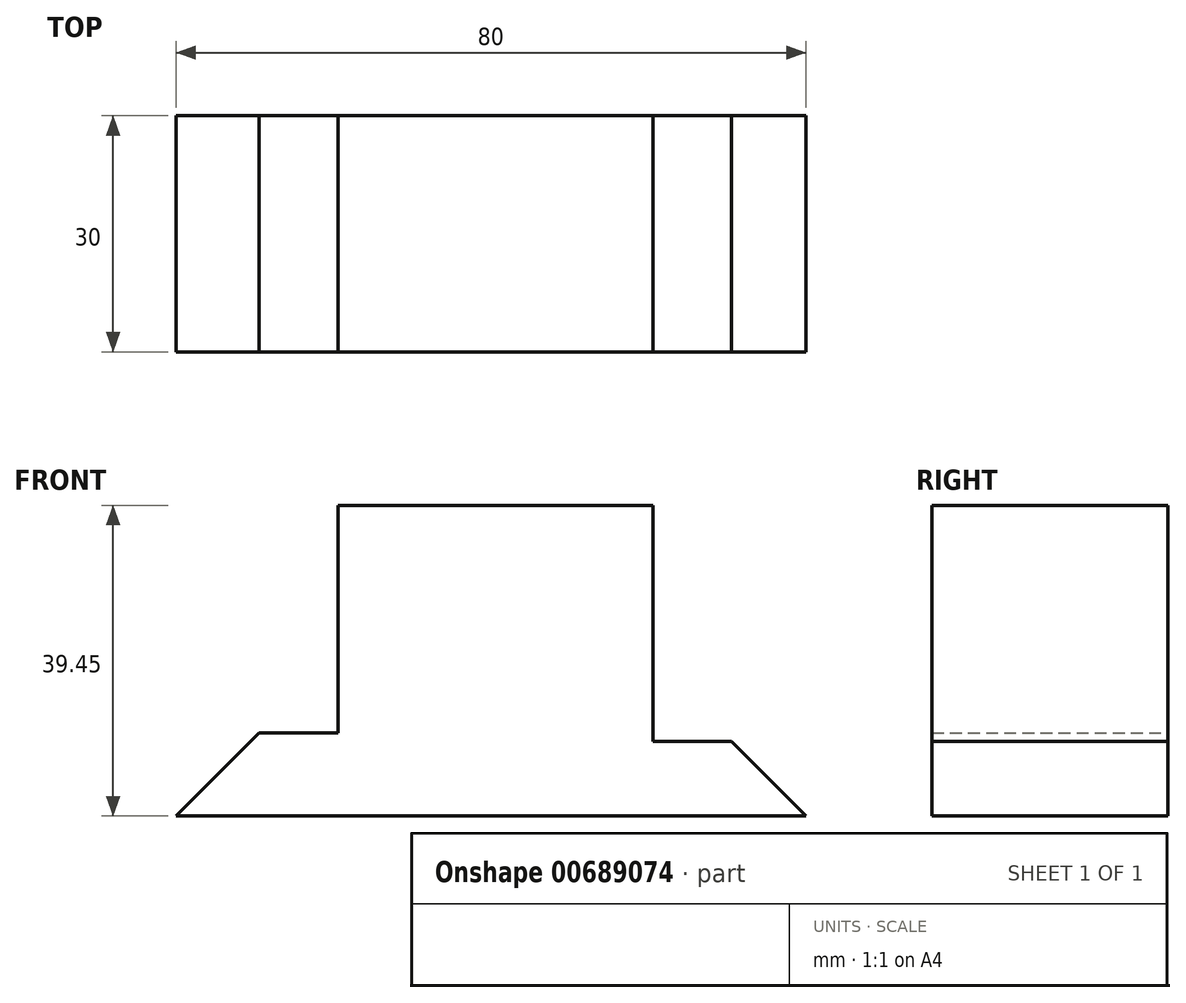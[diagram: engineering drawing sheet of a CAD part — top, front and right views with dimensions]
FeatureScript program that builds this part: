
annotation { "Feature Type Name" : "Feature", "Feature Type Description" : "" }
export const myFeature = defineFeature(function(context is Context, id is Id, definition is map)
    precondition{}
    {
        {
            var Q0;
            Q0=qCreatedBy(makeId("Front.planeOp"),FACE);
            var sketch = newSketch(context, id + "F0", { "sketchPlane" : qUnion([Q0])});
            skLineSegment(sketch, "E0", {"start": v(0, 0) * mm, "end": v(80, 0) * mm});
            skLineSegment(sketch, "E1", {"start": v(0, 0) * mm, "end": v(10.55, 10.55) * mm});
            skLineSegment(sketch, "E2", {"start": v(80, 0) * mm, "end": v(70.55, 9.45) * mm});
            skLineSegment(sketch, "E3", {"start": v(10.55, 10.55) * mm, "end": v(20.55, 10.55) * mm});
            skLineSegment(sketch, "E4", {"start": v(70.55, 9.45) * mm, "end": v(60.55, 9.45) * mm});
            skLineSegment(sketch, "E5", {"start": v(60.55, 9.45) * mm, "end": v(60.55, 39.45) * mm});
            skLineSegment(sketch, "E6", {"start": v(20.55, 10.55) * mm, "end": v(20.55, 39.45) * mm});
            skLineSegment(sketch, "E7", {"start": v(20.55, 39.45) * mm, "end": v(60.55, 39.45) * mm});
            skSolve(sketch);
        }
        {
            var Q0;
            Q0=makeQuery(id+"F0.imprint","IMPRINT",FACE,{"disambiguationData":[TD([[makeQuery(id+"F0.imprint","IMPRINT",EDGE,{"derivedFrom":sQuery(id+"F0.wireOp",EDGE,"E0")}),1.0]])]});
            extrude(context, id + "F1", {"entities" : qUnion([Q0]), "depth" : 30 * mm, "offsetDistance" : 25 * mm});
        }
    });
